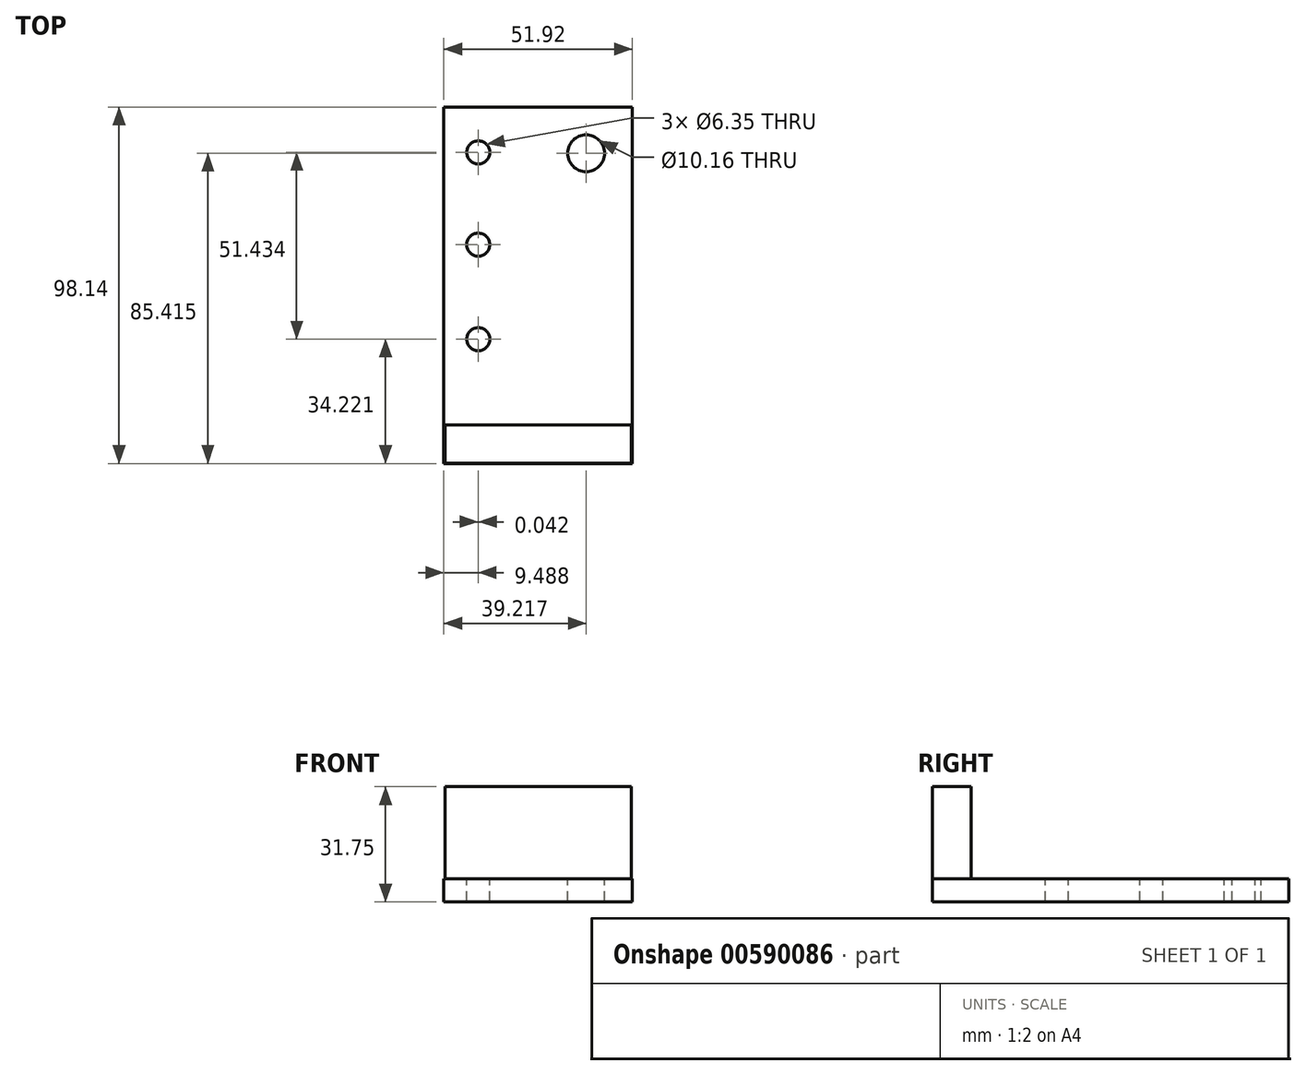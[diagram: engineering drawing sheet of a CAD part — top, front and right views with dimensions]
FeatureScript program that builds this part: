
annotation { "Feature Type Name" : "Feature", "Feature Type Description" : "" }
export const myFeature = defineFeature(function(context is Context, id is Id, definition is map)
    precondition{}
    {
        {
            var Q0;
            Q0=qCreatedBy(makeId("Top.planeOp"),FACE);
            var sketch = newSketch(context, id + "F0", { "sketchPlane" : qUnion([Q0])});
            skLineSegment(sketch, "E0.bottom", {"start": v(-16.24, -40.51) * mm, "end": v(35.68, -40.51) * mm});
            skLineSegment(sketch, "E0.top", {"start": v(-16.24, 57.63) * mm, "end": v(35.68, 57.63) * mm});
            skLineSegment(sketch, "E0.left", {"start": v(-16.24, -40.51) * mm, "end": v(-16.24, 57.63) * mm});
            skLineSegment(sketch, "E0.right", {"start": v(35.68, -40.51) * mm, "end": v(35.68, 57.63) * mm});
            skSolve(sketch);
        }
        {
            var Q0;
            Q0=qCreatedBy(makeId("Top.planeOp"),FACE);
            var sketch = newSketch(context, id + "F1", { "sketchPlane" : qUnion([Q0])});
            skLineSegment(sketch, "E1.bottom", {"start": v(-15.85, -40.5) * mm, "end": v(35.4, -40.5) * mm});
            skLineSegment(sketch, "E1.top", {"start": v(-15.85, -29.94) * mm, "end": v(35.4, -29.94) * mm});
            skLineSegment(sketch, "E1.left", {"start": v(-15.85, -40.5) * mm, "end": v(-15.85, -29.94) * mm});
            skLineSegment(sketch, "E1.right", {"start": v(35.4, -40.5) * mm, "end": v(35.4, -29.94) * mm});
            skSolve(sketch);
        }
        {
            var Q0;
            Q0=qSketchRegion(id+"F1",true);
            extrude(context, id + "F2", {"entities" : qUnion([Q0]), "depth" : 25.4 * mm, "offsetDistance" : 25.4 * mm});
        }
        {
            var Q0;
            Q0=qSketchRegion(id+"F0",true);
            extrude(context, id + "F3", {"entities" : qUnion([Q0]), "operationType" : NewBodyOperationType.ADD, "oppositeDirection" : true, "depth" : 6.35 * mm, "offsetDistance" : 25.4 * mm});
        }
        {
            var Q0;
            Q0=makeQuery(id+"F3.opExtrude","CAP_FACE",FACE,{"disambiguationData":[OSD([sQuery(id+"F0.wireOp",EDGE,"E0.bottom"),sQuery(id+"F0.wireOp",EDGE,"E0.top"),sQuery(id+"F0.wireOp",EDGE,"E0.left"),sQuery(id+"F0.wireOp",EDGE,"E0.right")])],"isStart":true});
            var sketch = newSketch(context, id + "F4", { "sketchPlane" : qUnion([Q0])});
            skCircle(sketch, "E2", {"center": v(-6.72, 45.15) * mm, "radius": 3.18 * mm});
            skCircle(sketch, "E3", {"center": v(-6.75, 19.75) * mm, "radius": 3.18 * mm});
            skCircle(sketch, "E4", {"center": v(-6.71, -6.29) * mm, "radius": 3.18 * mm});
            skCircle(sketch, "E5", {"center": v(22.98, 44.9) * mm, "radius": 5.08 * mm});
            skSolve(sketch);
        }
        {
            var Q0;
            Q0 = qSketchRegion(id + "F4", true);
            extrude(context, id + "F5", {"entities" : qUnion([Q0]), "operationType" : NewBodyOperationType.REMOVE, "oppositeDirection" : true, "depth" : 25.4 * mm, "offsetDistance" : 25.4 * mm});
        }
    });
